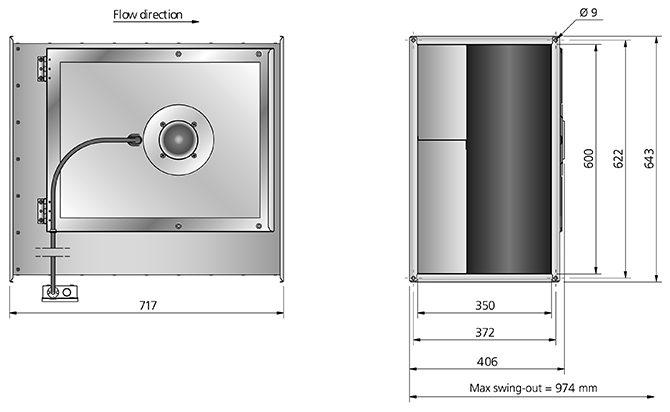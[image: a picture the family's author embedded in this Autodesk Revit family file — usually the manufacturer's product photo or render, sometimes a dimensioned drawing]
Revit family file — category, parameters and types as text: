
# Revit family: RKB 600X350 D1 ErP AC_7480162
name_source: partatom
category: Mechanical Equipment
revit_build: Autodesk Revit MEP 2014 (Build: 20130308_1515(x64)
units: mm (PartAtom-declared; Revit-internal decimal feet)

## types (1)
- RKB 600X350 D1 ErP AC
    Capacitor = 10 μF
    Connector Height = 350 mm  [stored 1.14829 ft]
    Connector Width = 600 mm
    Current = 3 A
    Depth = 643 mm  [stored 2.10958 ft]
    Description = UNINSULATED DUCT FANS WITH RECTANGULAR CONNECTIONS
    Frequency = 50 Hz
    Height = 406 mm  [stored 1.33202 ft]
    Main Material = Steel, Galvanized
    Max. temperature of transported air = 60 °C
    Max. temperature of transported air when speed controlled = 60 °C
    Phase = 1
    Power = 476 W
    Sound pressure level at 3 m = 57 dB(A)
    Speed = 1390 rpm
    Voltage = 230 V
    Voltage range = 220-240V
    Weight = 32.00 kg
    Width = 717 mm  [stored 2.35236 ft]
    Wiring diagram = 4040005

note: [stored X ft] marks values corroborated as IEEE doubles in the binary element streams (Revit-internal decimal feet)

## geometry (parser evidence)
native form markers: Sweep x4
no freeform markers — native parametric forms only
